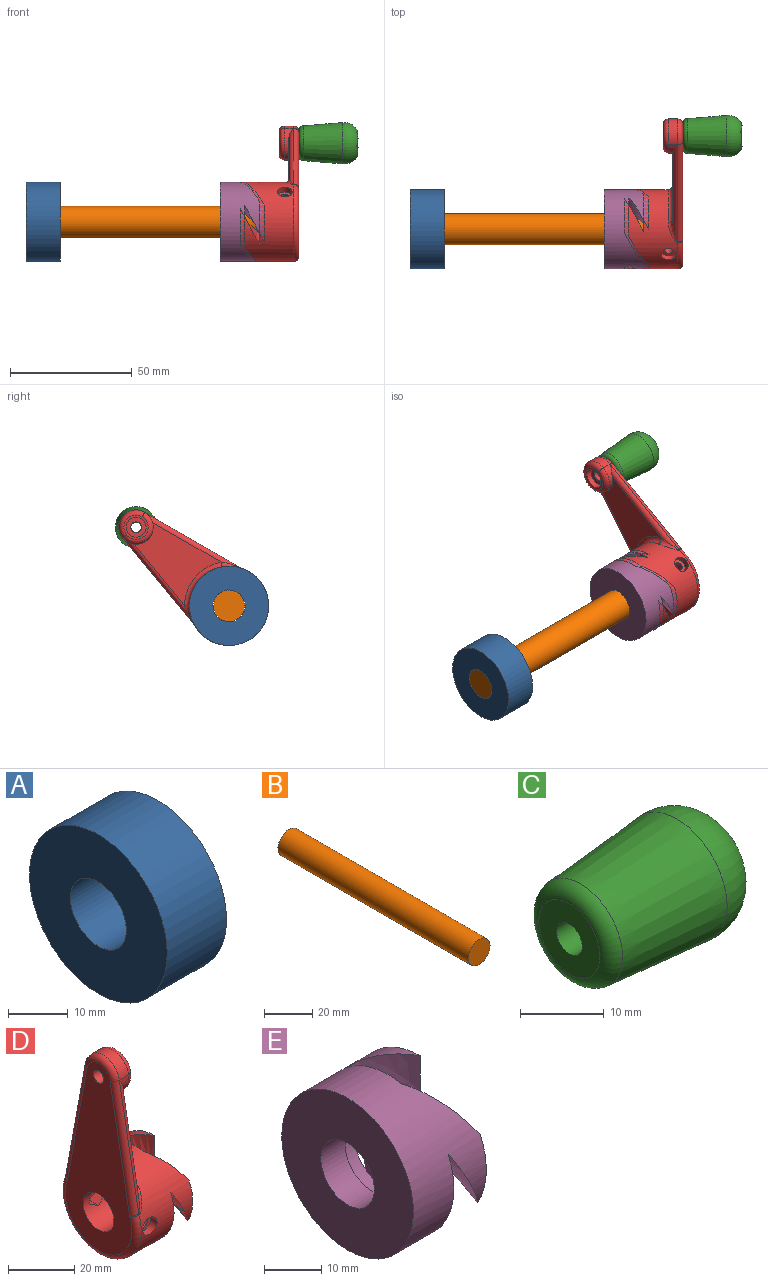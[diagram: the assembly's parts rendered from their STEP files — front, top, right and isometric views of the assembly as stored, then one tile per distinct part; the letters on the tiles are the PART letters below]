
ASSEMBLY  parts=5 mates=4
PART A: 4 faces, bbox 14x32.5x32.5 mm
  f0: cylinder r=6.6mm len=14mm, axis (-1,0,0), area 580.6mm2, adj f2,f3
  f1: cylinder r=16.25mm len=32.5mm, axis (-1,0,0), area 1429.4mm2, adj f2,f3
  f2: plane 32.5x32.5mm, normal (1,0,0), area 692.7mm2, adj f0,f1
  f3: plane 32.5x32.5mm, normal (-1,0,0), area 692.7mm2, adj f0,f1
PART B: 3 faces, bbox 12.8x112x12.8 mm
  f0: cylinder r=6.4mm len=112mm, axis (0,1,0), area 4503.8mm2, adj f1,f2
  f1: plane 12.8x12.8mm, normal (0,-1,0), area 128.7mm2, adj f0
  f2: plane 12.8x12.8mm, normal (0,1,0), area 128.7mm2, adj f0
PART C: 18 faces, bbox 25x17x17 mm
  f0: cylinder r=2.15mm len=10mm, axis (-1,0,0), area 135.1mm2, adj f2,f5
  f1: torus R=2.15mm, axis (-1,0,0), area 336.7mm2, adj f3,f12,f13,f14,f15,f16,f17
  f2: plane 10.32x10.32mm, normal (-1,0,0), area 69.1mm2, adj f0,f4
  f3: cone r=8.5mm half-angle=4.7deg, axis (1,0,0), area 802.7mm2, adj f1,f4
  f4: torus R=5.16mm, axis (1,0,0), area 119.5mm2, adj f2,f3
  f5: plane 8.43x7.3mm, normal (1,0,0), area 31.6mm2, adj f0,f6,f7,f8,f9,f10,f11
  f6: plane 13.38x3.65mm, normal (0,-0.5,0.87), area 56mm2, adj f5,f7,f11,f17
  f7: plane 13.38x4.22mm, normal (0,-1,0), area 56mm2, adj f5,f6,f8,f16
  f8: plane 13.38x3.65mm, normal (0,-0.5,-0.87), area 56mm2, adj f5,f7,f9,f14
  f9: plane 13.38x3.65mm, normal (0,0.5,-0.87), area 56mm2, adj f5,f8,f10,f12
  f10: plane 13.38x4.22mm, normal (0,1,0), area 56mm2, adj f5,f9,f11,f13
  f11: plane 13.38x3.65mm, normal (0,0.5,0.87), area 56mm2, adj f5,f6,f10,f15
  f12: bspline ~7.9x5.43mm, area 11mm2, adj f1,f9,f13,f14
  f13: bspline ~8.68x2.52mm, area 11mm2, adj f1,f10,f12,f15
  f14: bspline ~7.86x5.45mm, area 11mm2, adj f1,f8,f12,f16
  f15: bspline ~7.86x5.45mm, area 11mm2, adj f1,f11,f13,f17
  f16: bspline ~8.68x2.52mm, area 11mm2, adj f1,f7,f14,f17
  f17: bspline ~7.9x5.43mm, area 11mm2, adj f1,f6,f15,f16
PART D: 57 faces, bbox 24.1x35.3x75.5 mm
  f0: cylinder r=4.1mm len=8.2mm, axis (-1,0,0), area 64.4mm2, adj f42,f56
  f1: plane 32.03x23.3mm, normal (1,0,0), area 466.9mm2, adj f41,f44,f46,f50
  f2: cylinder r=16.25mm len=32.5mm, axis (-1,0,0), area 1620.5mm2, adj f5,f6,f7,f8,f9,f10,f11,f12
  f3: cylinder r=1.7mm len=3.65mm, axis (0,1,0), area 39mm2, adj f35,f40
  f4: cylinder r=6.6mm len=13.2mm, axis (-1,0,0), area 435.1mm2, adj f18,f21,f23,f24,f25,f26,f27,f28
  f5: bspline ~14.74x8.67mm, area 107.1mm2, adj f2,f6,f9,f17
  f6: plane 14.99x8.67mm, normal (1,0,0), area 90mm2, adj f2,f5,f7,f17
  f7: bspline ~13.06x12.25mm, area 107.2mm2, adj f2,f6,f8,f17
  f8: plane 16.26x11.12mm, normal (1,0,0), area 106.4mm2, adj f2,f7,f12,f17
  f9: plane 17.28x9.65mm, normal (1,0,0), area 106.4mm2, adj f2,f5,f14,f17
  f10: plane 13.31x11.23mm, normal (1,0,0), area 90mm2, adj f2,f11,f12,f17
  f11: bspline ~14.62x9.08mm, area 107.2mm2, adj f2,f10,f16,f17
  f12: bspline ~16.25x15.84mm, area 107.1mm2, adj f2,f8,f10,f17
  f13: plane 13.31x11.81mm, normal (1,0,0), area 90mm2, adj f2,f14,f15,f17
  f14: bspline ~16.88x16.51mm, area 107.2mm2, adj f2,f9,f13,f17
  f15: bspline ~18.86x16.62mm, area 107.2mm2, adj f2,f13,f16,f17
  f16: plane 14.46x13.32mm, normal (1,0,0), area 106.3mm2, adj f2,f11,f15,f17
  f17: cylinder r=8.75mm len=17.5mm, axis (1,0,0), area 421.6mm2, adj f5,f6,f7,f8,f9,f10,f11,f12
  f18: plane 17.5x17.5mm, normal (1,0,0), area 103.7mm2, adj f4,f17
  f19: cylinder r=7mm len=13.77mm, axis (1,0,0), area 77.8mm2, adj f41,f52,f55
  f20: cylinder r=2.2mm len=5.5mm, axis (1,0,0), area 76mm2, adj f21,f56
  f21: plane 69.25x28.5mm, normal (-1,0,0), area 1173.2mm2, adj f4,f20,f45,f48,f49,f51,f52,f53
  f22: plane 6.81x5.9mm, normal (0,-1,0), area 21.1mm2, adj f23,f24,f25,f26,f27,f28,f37
  f23: plane 4.29x3.04mm, normal (0.5,0,-0.87), area 12.9mm2, adj f4,f22,f24,f28
  f24: plane 4.29x3.04mm, normal (-0.5,0,-0.87), area 12.9mm2, adj f4,f22,f23,f25
  f25: plane 3.47x3.41mm, normal (-1,0,0), area 11.3mm2, adj f4,f22,f24,f26
  f26: plane 4.29x3.04mm, normal (-0.5,0,0.87), area 12.9mm2, adj f4,f22,f25,f27
  f27: plane 4.29x3.04mm, normal (0.5,0,0.87), area 12.9mm2, adj f4,f22,f26,f28
  f28: plane 3.47x3.41mm, normal (1,0,0), area 11.3mm2, adj f4,f22,f23,f27
  f29: plane 4.29x3.04mm, normal (-0.5,0,-0.87), area 12.9mm2, adj f4,f30,f34,f35
  f30: plane 4.29x3.04mm, normal (0.5,0,-0.87), area 12.9mm2, adj f4,f29,f31,f35
  f31: plane 3.47x3.41mm, normal (1,0,0), area 11.3mm2, adj f4,f30,f32,f35
  f32: plane 4.29x3.04mm, normal (0.5,0,0.87), area 12.9mm2, adj f4,f31,f33,f35
  f33: plane 4.29x3.04mm, normal (-0.5,0,0.87), area 12.9mm2, adj f4,f32,f34,f35
  f34: plane 3.47x3.41mm, normal (-1,0,0), area 11.3mm2, adj f4,f29,f33,f35
  f35: plane 6.81x5.9mm, normal (0,1,0), area 21.1mm2, adj f3,f29,f30,f31,f32,f33,f34
  f36: cylinder r=3.05mm len=6.1mm, axis (0,1,0), area 47.2mm2, adj f2,f38
  f37: cylinder r=1.7mm len=3.65mm, axis (0,1,0), area 39mm2, adj f22,f38
  f38: plane 6.1x6.1mm, normal (0,1,0), area 20.1mm2, adj f36,f37
  f39: cylinder r=3.05mm len=6.1mm, axis (0,-1,0), area 47.2mm2, adj f2,f40
  f40: plane 6.1x6.1mm, normal (0,-1,0), area 20.1mm2, adj f3,f39
  f41: extruded ~13.99x8.26mm, area 59.9mm2, adj f1,f19,f46,f50,f54
  f42: plane 10.01x10mm, normal (1,0,0), area 25.7mm2, adj f0,f54,f55
  f43: bspline ~9.1x5.55mm, area 16.2mm2, adj f2,f44,f45,f46
  f44: torus R=18.25mm, axis (-1,0,0), area 73.9mm2, adj f1,f2,f43,f47
  f45: torus R=4mm, axis (-1,0,0), area 1.5mm2, adj f21,f43,f48,f49
  f46: cylinder r=2mm len=45.7mm, axis (0,0.18,-0.98), area 123.5mm2, adj f1,f41,f43,f49
  f47: bspline ~9.36x5.83mm, area 16.2mm2, adj f2,f44,f50,f51
  f48: torus R=14.25mm, axis (-1,0,0), area 187.5mm2, adj f2,f21,f45,f51
  f49: cylinder r=2mm len=45.7mm, axis (0,-0.18,0.98), area 144.8mm2, adj f21,f45,f46,f52
  f50: cylinder r=2mm len=45.7mm, axis (0,0.18,0.98), area 123.5mm2, adj f1,f41,f47,f53
  f51: torus R=4mm, axis (-1,0,0), area 1.5mm2, adj f21,f47,f48,f53
  f52: torus R=5mm, axis (-1,0,0), area 54.8mm2, adj f19,f21,f49,f53
  f53: cylinder r=2mm len=45.7mm, axis (0,-0.18,-0.98), area 144.8mm2, adj f21,f50,f51,f52
  f54: bspline ~14.81x14.02mm, area 69mm2, adj f41,f42,f55
  f55: torus R=5mm, axis (1,0,0), area 54.8mm2, adj f19,f42,f54
  f56: plane 8.2x8.2mm, normal (1,0,0), area 37.6mm2, adj f0,f20
PART E: 17 faces, bbox 18x32.5x32.9 mm
  f0: cylinder r=6.6mm len=13.2mm, axis (-1,0,0), area 248.8mm2, adj f13,f16
  f1: bspline ~14.74x8.67mm, area 107.1mm2, adj f2,f3,f6,f15
  f2: cylinder r=16.25mm len=32.5mm, axis (-1,0,0), area 1395.3mm2, adj f1,f3,f4,f5,f6,f7,f8,f9
  f3: plane 14.99x8.67mm, normal (1,0,0), area 90mm2, adj f1,f2,f4,f15
  f4: bspline ~13.06x12.25mm, area 107.2mm2, adj f2,f3,f5,f15
  f5: plane 16.26x11.12mm, normal (1,0,0), area 106.4mm2, adj f2,f4,f9,f15
  f6: plane 17.28x9.65mm, normal (1,0,0), area 106.4mm2, adj f1,f2,f11,f15
  f7: plane 13.31x11.23mm, normal (1,0,0), area 90mm2, adj f2,f8,f9,f15
  f8: bspline ~14.62x9.08mm, area 107.2mm2, adj f2,f7,f14,f15
  f9: bspline ~16.25x15.84mm, area 107.1mm2, adj f2,f5,f7,f15
  f10: plane 13.31x11.81mm, normal (1,0,0), area 90mm2, adj f2,f11,f12,f15
  f11: bspline ~16.88x16.51mm, area 107.2mm2, adj f2,f6,f10,f15
  f12: bspline ~18.86x16.62mm, area 107.2mm2, adj f2,f10,f14,f15
  f13: plane 32.5x32.5mm, normal (-1,0,0), area 692.7mm2, adj f0,f2
  f14: plane 14.46x13.32mm, normal (1,0,0), area 106.3mm2, adj f2,f8,f12,f15
  f15: cylinder r=8.75mm len=17.5mm, axis (1,0,0), area 421.6mm2, adj f1,f3,f4,f5,f6,f7,f8,f9
  f16: plane 17.5x17.5mm, normal (1,0,0), area 103.7mm2, adj f0,f15
PLACE A rot(axis=(-1,0,0),49.8deg) t=(-79.89,0,0)mm
PLACE B rot(axis=(-0.68,-0.68,-0.25),151.8deg) t=(32.11,0,0)mm
PLACE C rot(axis=(1,0,0),40.2deg) t=(32.11,38.17,32.29)mm
PLACE D rot(axis=(0,0.42,0.91),180deg) t=(16.11,0,0)mm
PLACE E rot(axis=(1,0,0),0deg) t=(10,0,0)mm
MATE cylindrical E.f2 <-> B.f0  axis (-1,0,0) through (0,0,0)mm
MATE revolute D.f20 <-> C.f0  axis (1,0,0) through (32.11,38.17,32.29)mm
MATE fastened B.f0 <-> D.f4  axis (1,0,0) through (32.11,0,0)mm
MATE fastened B.f0 <-> A.f1  axis (-1,0,0) through (-79.89,0,0)mm
